# Revit family: GR_Адаптер линейный_Муфта(1)_SDL-КСД-У-П_R21
name_source: partatom
category: Соединительные детали воздуховодов
units: mm (PartAtom-declared; Revit-internal decimal feet)

## family parameters
Всегда вертикально = Да
Заголовок OmniClass = Metal Ducts
На основе рабочей плоскости = Нет
Номер OmniClass = 23.75.70.14.31
Общий = Нет
При загрузке вырезать с полостями = Нет
Размер круглого соединителя = Использовать диаметр
Тип детали = Мультипорт

## types (6) — shared parameters
ADSK_URL страницы изделия = https://grilles.ru
ADSK_Версия Revit = 2021
ADSK_Единица измерения = шт.
ADSK_Завод-изготовитель = ООО "ВЕНТРЕШЕТКИКОМ"
ADSK_Код изделия = 000192
ADSK_Количество = 1
ADSK_Материал = ADSK_Оцинкованная сталь
ADSK_Наименование = SDL-КСД-У-П, адаптер вентиляционной решётки
Изготовитель = ООО "ВЕНТРЕШЕТКИКОМ"
Корпус_Металл_Толщина = 1 мм
Муфта_Металл_Толщина = 1 мм
zero-valued in all types: Отметка по умолчанию

## per-type parameters (varying)
| type | Корпус_Высота | Корпус_Длина | Муфта_Отступ_ОВ_2 | Решетка_отступ | Решётка_Высота |
| SDL-КСД-У-П 1-20 | 75 мм | 171 мм | 86 мм | 25 мм | 48 мм |
| SDL-КСД-У-П 2-20 | 105 мм | 209 мм | 105 мм | 44 мм | 86 мм |
| SDL-КСД-У-П 3-20 | 105 мм | 247 мм | 124 мм | 63 мм | 124 мм |
| SDL-КСД-У-П 4-20 | 140 мм | 285 мм | 143 мм | 82 мм | 162 мм |
| SDL-КСД-У-П 5-20 | 140 мм | 323 мм | 162 мм | 101 мм | 200 мм |
| SDL-КСД-У-П 6-20 | 175 мм | 361 мм | 181 мм | 120 мм | 238 мм |

note: column(s) folded — value = type name in every type: ADSK_Марка
